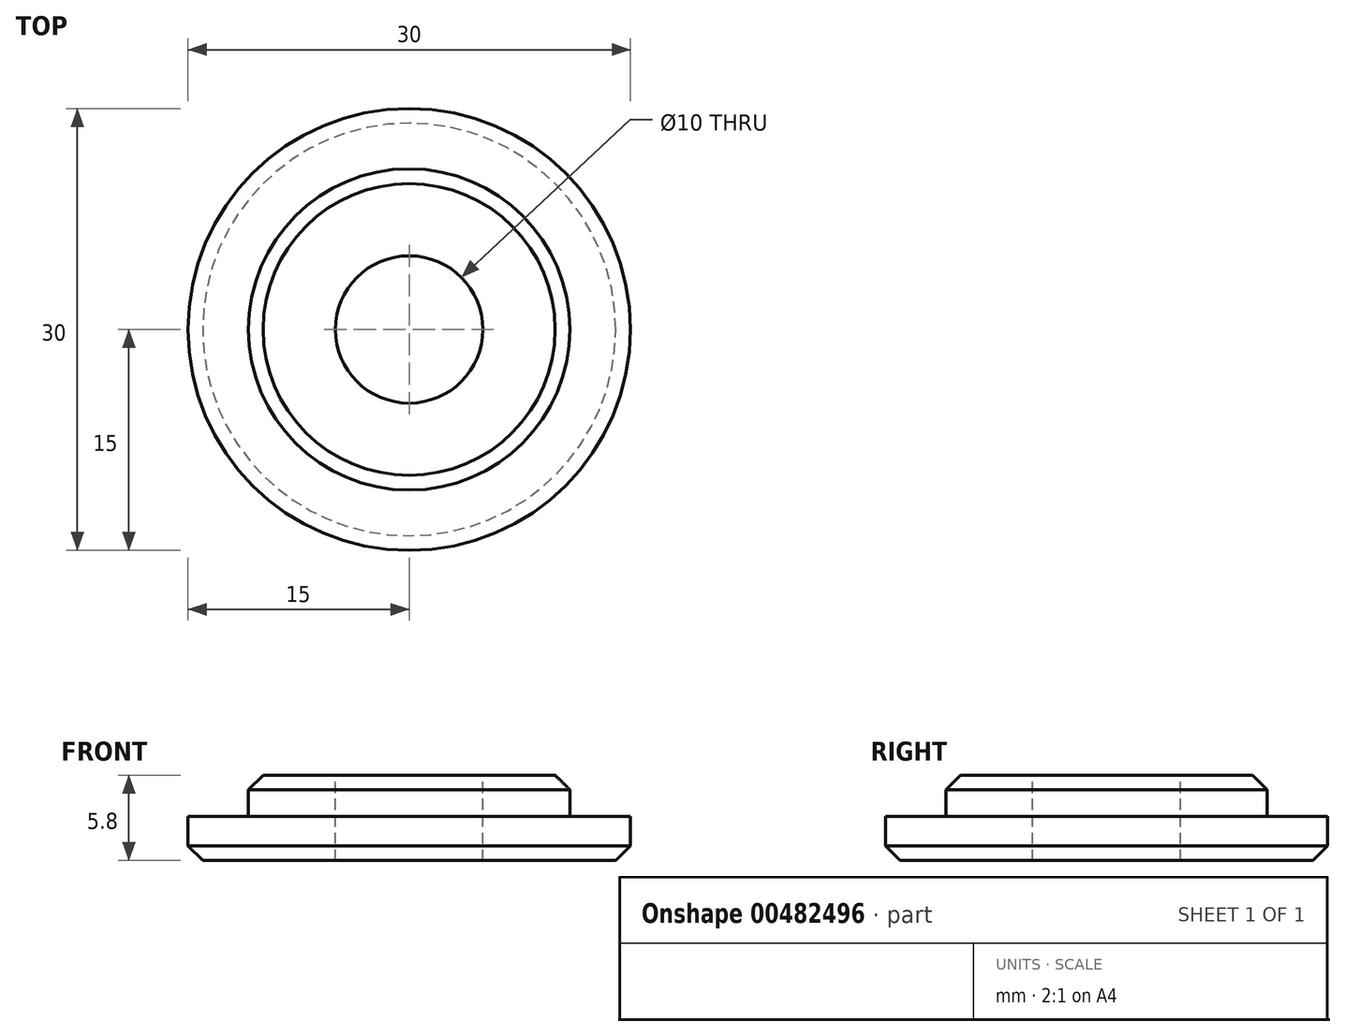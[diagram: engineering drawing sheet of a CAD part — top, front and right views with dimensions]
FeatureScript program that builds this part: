
annotation { "Feature Type Name" : "Feature", "Feature Type Description" : "" }
export const myFeature = defineFeature(function(context is Context, id is Id, definition is map)
    precondition{}
    {
        {
            var Q0;
            Q0=qCreatedBy(makeId("Top.planeOp"),FACE);
            var sketch = newSketch(context, id + "F0", { "sketchPlane" : qUnion([Q0])});
            skCircle(sketch, "E0", {"center": v(0, 0) * mm, "radius": 15 * mm});
            skSolve(sketch);
        }
        {
            var Q0;
            Q0 = qSketchRegion(id + "F0", true);
            extrude(context, id + "F1", {"entities" : qUnion([Q0]), "depth" : 3 * mm});
        }
        {
            var Q0;
            Q0=qCreatedBy(makeId("Top.planeOp"),FACE);
            var sketch = newSketch(context, id + "F2", { "sketchPlane" : qUnion([Q0])});
            skCircle(sketch, "E1", {"center": v(0, 0) * mm, "radius": 10.9 * mm});
            skCircle(sketch, "E2", {"center": v(0, 0) * mm, "radius": 5 * mm});
            skSolve(sketch);
        }
        {
            var Q0;
            Q0 = qSketchRegion(id + "F2", true);
            extrude(context, id + "F3", {"entities" : qUnion([Q0]), "operationType" : NewBodyOperationType.ADD, "depth" : 5.8 * mm});
        }
        {
            var Q0;
            Q0=makeQuery(id+"F3.boolean.opBoolean","SPLIT",FACE,{"disambiguationData":[TD([makeQuery(id+"F3.opExtrude","SWEPT_FACE",FACE,{"disambiguationData":[OSD([sQuery(id+"F2.wireOp",EDGE,"E2")])]})])],"derivedFrom":makeQuery(id+"F1.opExtrude","CAP_FACE",FACE,{"disambiguationData":[OSD([sQuery(id+"F0.wireOp",EDGE,"E0")])],"isStart":false})});
            extrude(context, id + "F4", {"entities" : qUnion([Q0]), "operationType" : NewBodyOperationType.ADD, "depth" : 25 * mm});
        }
        {
            var Q0;
            Q0=makeQuery(id+"F4.opExtrude","CAP_FACE",FACE,{"disambiguationData":[OSD([sQuery(id+"F0.wireOp",EDGE,"E0")])],"isStart":false});
            extrude(context, id + "F5", {"entities" : qUnion([Q0]), "operationType" : NewBodyOperationType.REMOVE, "oppositeDirection" : true, "depth" : 40.4 * mm});
        }
        {
            var Q0;
            Q0=makeQuery(id+"F1.opExtrude","CAP_EDGE",EDGE,{"disambiguationData":[OSD([sQuery(id+"F0.wireOp",EDGE,"E0")])],"isStart":true});
            var Q1;
            Q1=makeQuery(id+"F3.opExtrude","CAP_EDGE",EDGE,{"disambiguationData":[OSD([sQuery(id+"F2.wireOp",EDGE,"E1")])],"isStart":false});
            chamfer(context, id + "F6", {"entities" : qUnion([Q0, Q1]), "width" : 1 * mm, "tangentPropagation" : true});
        }
    });
